# Revit family: AFX-Jaxx-LED_Pendant
name_source: partatom
category: Lighting Fixtures
units: mm (PartAtom-declared; Revit-internal decimal feet)

## family parameters
Cut with Voids When Loaded = No
Host = Face
Light Source = No
Part Type = Normal
Room Calculation Point = No
Round Connector Dimension = Use Diameter
Shared = No

## types (1)
- JAXP24L30D1BK
    Apparent Load = 0 VA
    Assembly Code = D5020200
    Body Finish = AFX - Powdercoat Black
    Cable Finish = AFX - Powdercoat Black
    Canopy Finish = AFX - Powdercoat Black
    Color Rendering Index = 90
    Default Elevation = 48"
    Description = LED Pendant Black - 24"Dia x 11 1/2"H - 48 Pulg Max
    Diameter = 24"
    Height = 11 1/2"
    Keynote = 12500
    Lamp = LED
    Manufacturer = AFX Inc
    Model = JAXP24L30D1BK
    Product Documentation Link = https://www.afxinc.com
    Revit Model Built By = https://servex-us.com
    Screen Finish = AFX - Diffuser
    Type Comments = JAXX
    URL = https://www.afxinc.com
    Voltage = 120 V
    Wattage Comments = 40W

## geometry (parser evidence)
native form markers: Sweep x4
no freeform markers — native parametric forms only
